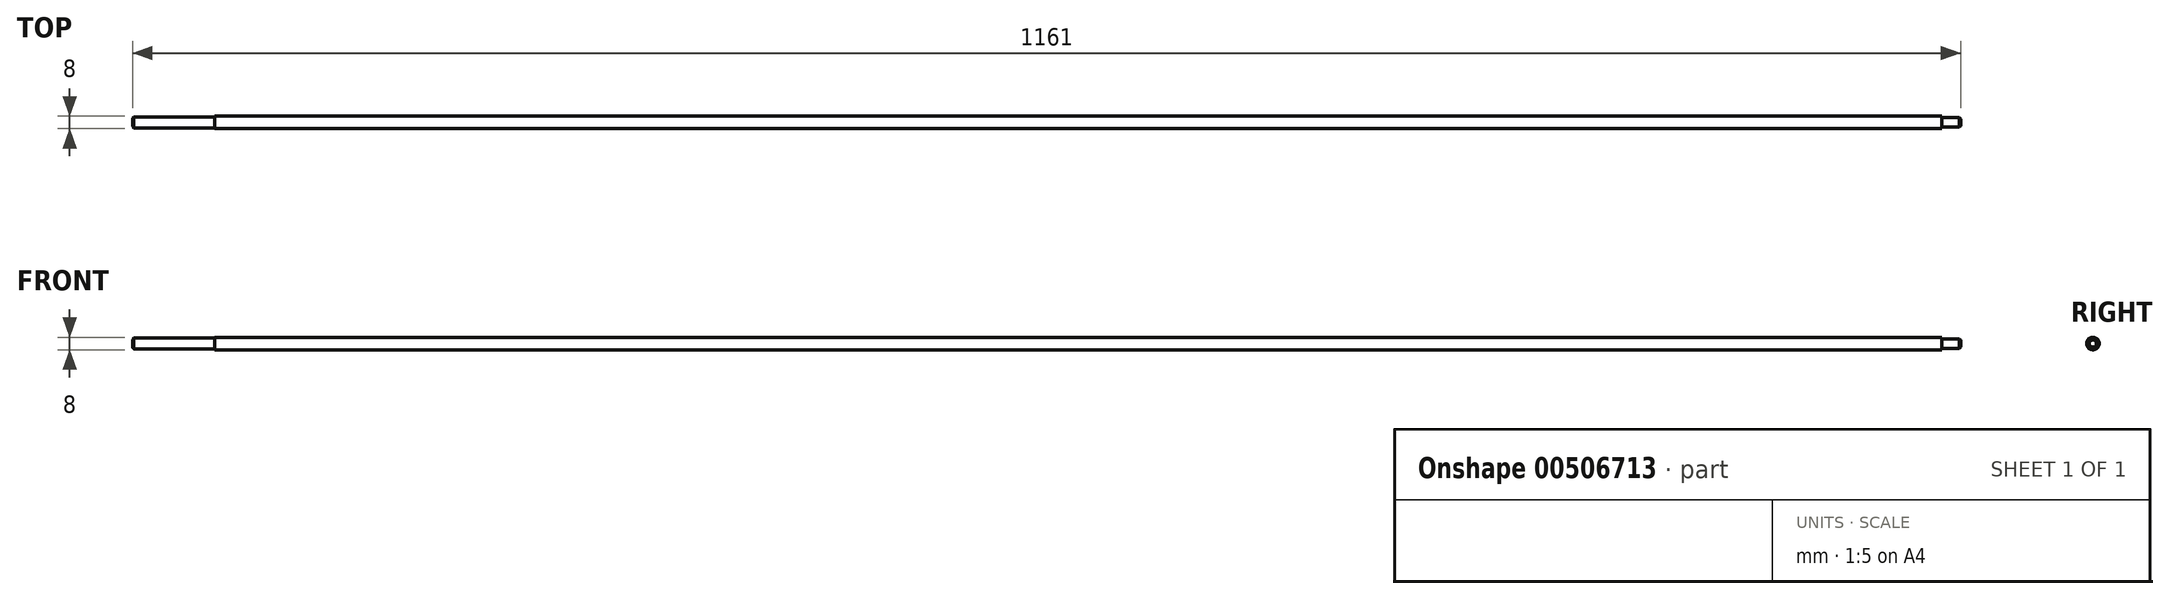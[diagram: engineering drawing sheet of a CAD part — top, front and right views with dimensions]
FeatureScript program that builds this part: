
annotation { "Feature Type Name" : "Feature", "Feature Type Description" : "" }
export const myFeature = defineFeature(function(context is Context, id is Id, definition is map)
    precondition{}
    {
        {
            var Q0;
            Q0=qCreatedBy(makeId("Right.planeOp"),FACE);
            var sketch = newSketch(context, id + "F0", { "sketchPlane" : qUnion([Q0])});
            skCircle(sketch, "E0", {"center": v(0, 0) * mm, "radius": 4 * mm});
            skSolve(sketch);
        }
        {
            var Q0;
            Q0=qSketchRegion(id+"F0",true);
            extrude(context, id + "F1", {"entities" : qUnion([Q0]), "depth" : 1097 * mm});
        }
        {
            var Q0;
            Q0=qCreatedBy(makeId("Right.planeOp"),FACE);
            var sketch = newSketch(context, id + "F2", { "sketchPlane" : qUnion([Q0])});
            skCircle(sketch, "E1", {"center": v(0, 0) * mm, "radius": 3.5 * mm});
            skSolve(sketch);
        }
        {
            var Q0;
            Q0=qSketchRegion(id+"F2",true);
            extrude(context, id + "F3", {"entities" : qUnion([Q0]), "operationType" : NewBodyOperationType.ADD, "oppositeDirection" : true, "depth" : 52 * mm});
        }
        {
            var Q0;
            Q0=makeQuery(id+"F1.opExtrude","CAP_FACE",FACE,{"disambiguationData":[OSD([sQuery(id+"F0.wireOp",EDGE,"E0")])],"isStart":false});
            var sketch = newSketch(context, id + "F4", { "sketchPlane" : qUnion([Q0])});
            skCircle(sketch, "E2", {"center": v(0, 0) * mm, "radius": 3 * mm});
            skSolve(sketch);
        }
        {
            var Q0;
            Q0=qSketchRegion(id+"F4",true);
            extrude(context, id + "F5", {"entities" : qUnion([Q0]), "operationType" : NewBodyOperationType.ADD, "depth" : 12 * mm});
        }
        {
            var Q0;
            Q0=makeQuery(id+"F5.opExtrude","CAP_EDGE",EDGE,{"disambiguationData":[OSD([sQuery(id+"F4.wireOp",EDGE,"E2")])],"isStart":false});
            chamfer(context, id + "F6", {"entities" : qUnion([Q0]), "width" : .75 * mm, "tangentPropagation" : true});
        }
        {
            var Q0;
            Q0=makeQuery(id+"F3.opExtrude","CAP_EDGE",EDGE,{"disambiguationData":[OSD([sQuery(id+"F2.wireOp",EDGE,"E1")])],"isStart":false});
            chamfer(context, id + "F7", {"entities" : qUnion([Q0]), "width" : .75 * mm, "tangentPropagation" : true});
        }
    });
